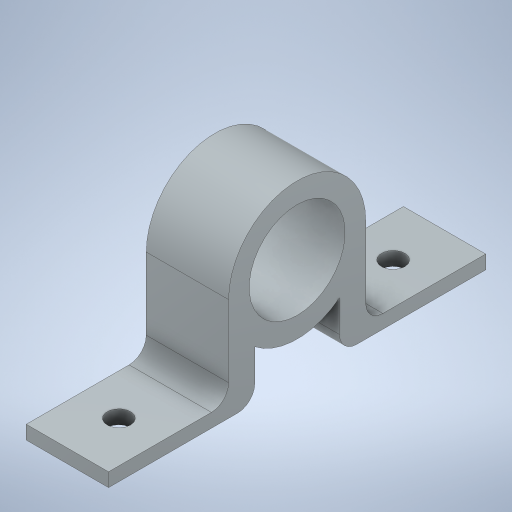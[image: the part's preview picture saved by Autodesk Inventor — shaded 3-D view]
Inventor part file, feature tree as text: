
AUTODESK INVENTOR PART (.ipt)
format: ipt  version: 2024 (Build 280153020, 153B)  size: 293,376 bytes
history: native  units: mm
features: extrude x3, sketch x3
ambient origin geometry x8: Origin, YZ Plane, XZ Plane, XY Plane, X Axis, Y Axis, Z Axis, Center Point
bodies: Solid1 (feature_tree)
feature tree (6):
  extrude  "Extrusion1"  Depth=3.0mm
  extrude  "Extrusion2"  Depth=2.5mm
  extrude  "Extrusion3"  Depth=12.0mm
  sketch  "Sketch1"  dims[d0=14.0mm d1=3.0mm]
  sketch  "Sketch2"  dims[d2=13.0mm d4=2.5mm]
  sketch  "Sketch3"  dims[d5=12.0mm d6=0.0mm d7=15.0mm d8=3.4mm d9=12.0mm d10=0.0mm d11=3.4mm d12=12.0mm d13=0.0mm]
